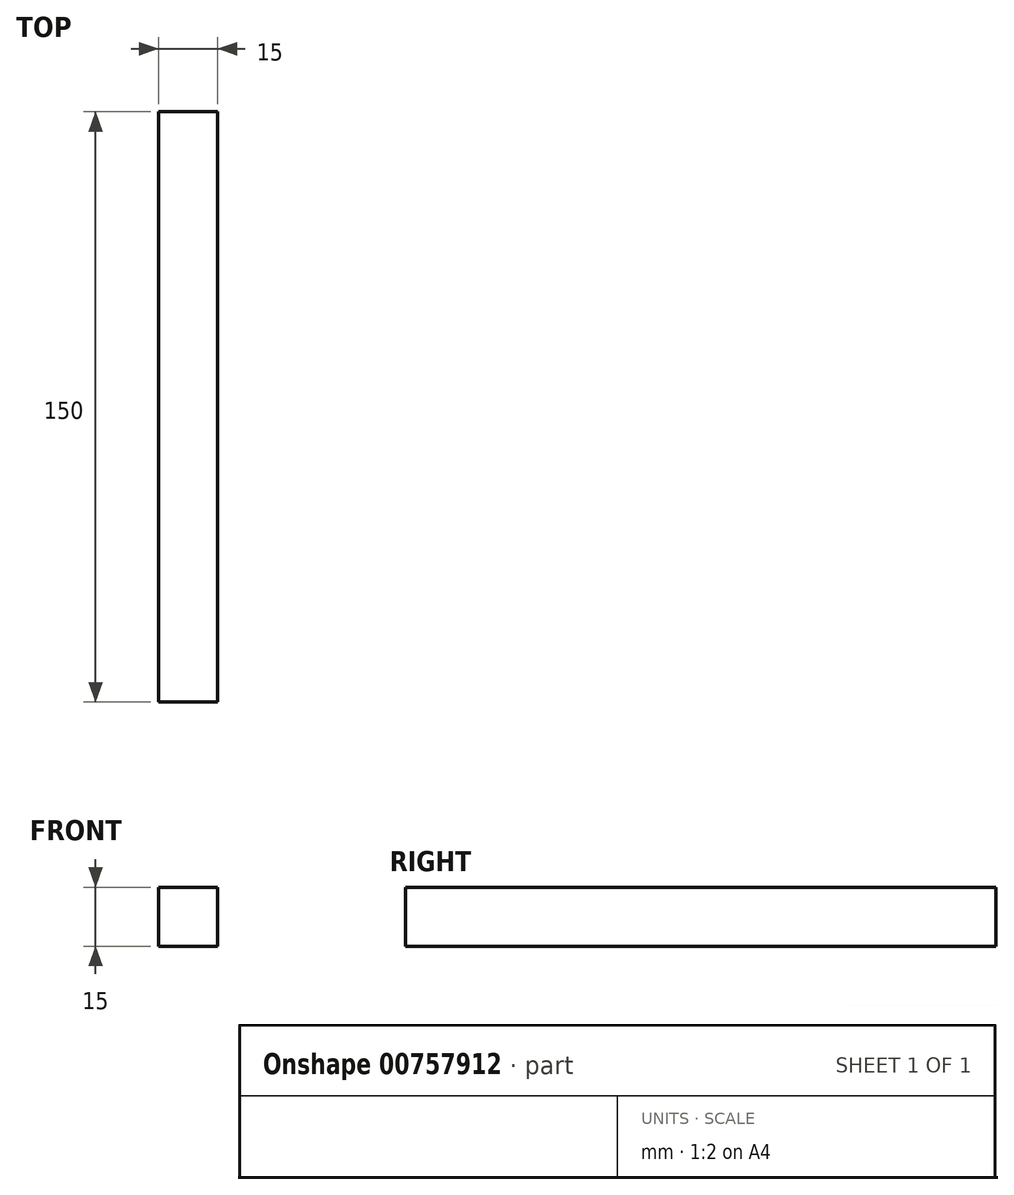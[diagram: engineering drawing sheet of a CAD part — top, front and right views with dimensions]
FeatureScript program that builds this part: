
annotation { "Feature Type Name" : "Feature", "Feature Type Description" : "" }
export const myFeature = defineFeature(function(context is Context, id is Id, definition is map)
    precondition{}
    {
        {
            var Q0;
            Q0=qCreatedBy(makeId("Top.planeOp"),FACE);
            var sketch = newSketch(context, id + "F0", { "sketchPlane" : qUnion([Q0])});
            skLineSegment(sketch, "E0.bottom", {"start": v(-7.5, 75) * mm, "end": v(7.5, 75) * mm});
            skLineSegment(sketch, "E0.top", {"start": v(-7.5, -75) * mm, "end": v(7.5, -75) * mm});
            skLineSegment(sketch, "E0.left", {"start": v(-7.5, 75) * mm, "end": v(-7.5, -75) * mm});
            skLineSegment(sketch, "E0.right", {"start": v(7.5, 75) * mm, "end": v(7.5, -75) * mm});
            skPoint(sketch, "E0.middle", {"position": v(0, 0) * mm});
            skSolve(sketch);
        }
        {
            var Q0;
            Q0=makeQuery(id+"F0.imprint","IMPRINT",FACE,{"disambiguationData":[TD([[makeQuery(id+"F0.imprint","IMPRINT",EDGE,{"derivedFrom":sQuery(id+"F0.wireOp",EDGE,"E0.bottom")}),-1.0]])]});
            extrude(context, id + "F1", {"entities" : qUnion([Q0]), "depth" : 15 * mm, "offsetDistance" : 25 * mm});
        }
    });
